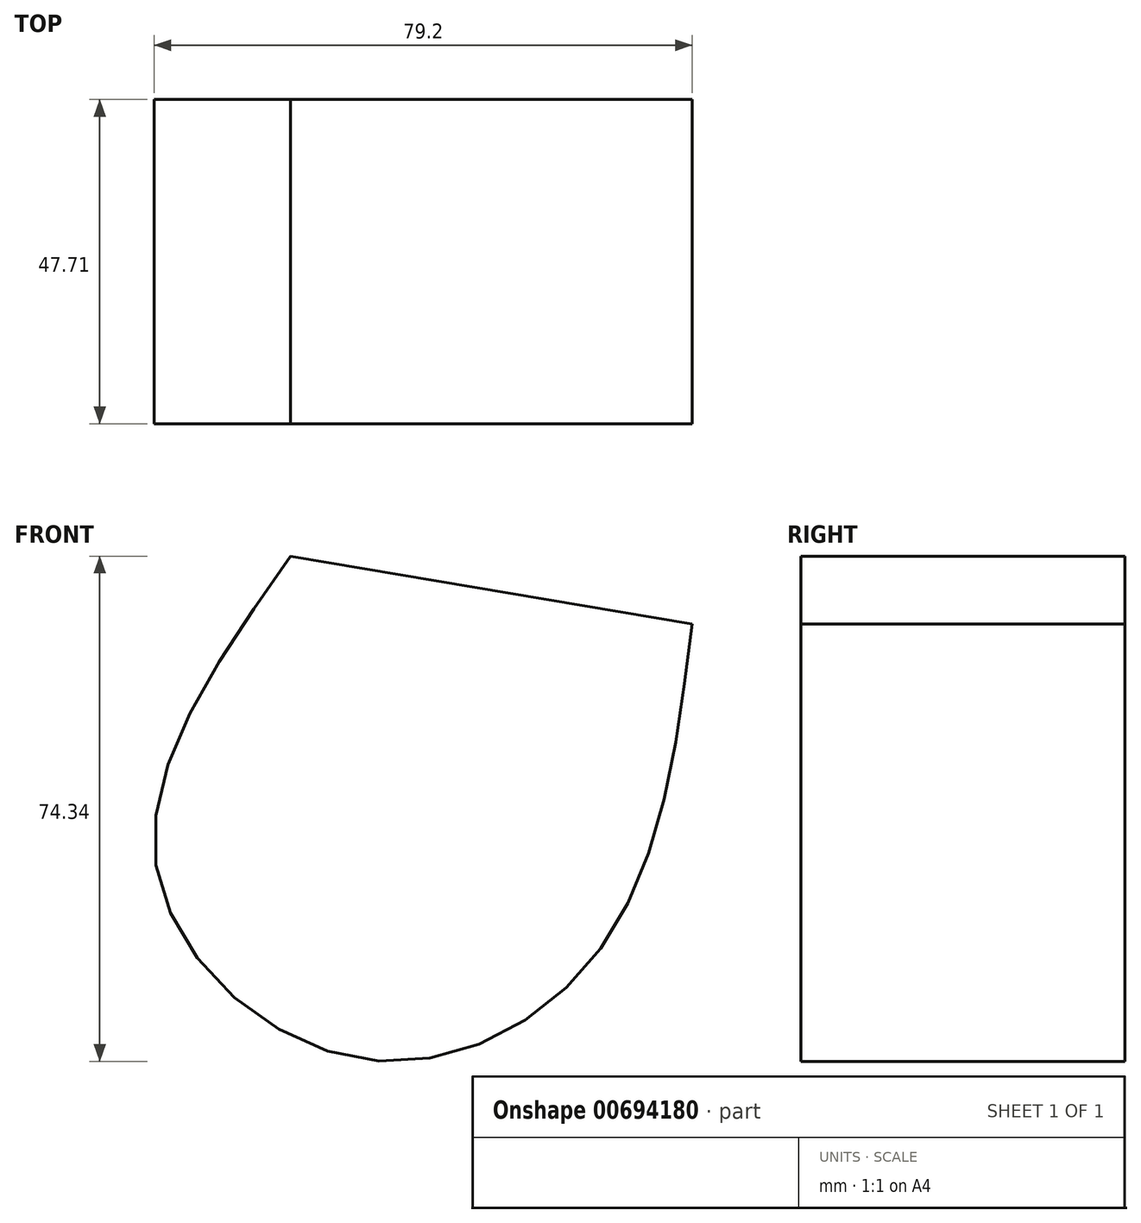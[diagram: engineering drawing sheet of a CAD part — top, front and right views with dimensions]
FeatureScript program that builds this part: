
annotation { "Feature Type Name" : "Feature", "Feature Type Description" : "" }
export const myFeature = defineFeature(function(context is Context, id is Id, definition is map)
    precondition{}
    {
        {
            var Q0;
            Q0=qCreatedBy(makeId("Front.planeOp"),FACE);
            var sketch = newSketch(context, id + "F0", { "sketchPlane" : qUnion([Q0])});
            skFitSpline(sketch, "E0", {"points": [v(-27.18, 23.86) * mm, v(-46.89, -22.2) * mm, v(-17.63, -50) * mm, v(18.05, -34.44) * mm, v(31.95, 13.9) * mm], "startDerivative": vector(-126.13, -178.37) * mm, "endDerivative": vector(25.2, 202.46) * mm});
            skLineSegment(sketch, "E1", {"start": v(31.95, 13.9) * mm, "end": v(-27.18, 23.86) * mm});
            skSolve(sketch);
        }
        {
            var Q0;
            Q0=makeQuery(id+"F0.imprint","IMPRINT",FACE,{"disambiguationData":[TD([[makeQuery(id+"F0.imprint","IMPRINT",EDGE,{"derivedFrom":sQuery(id+"F0.wireOp",EDGE,"E0")}),1.0]])]});
            extrude(context, id + "F1", {"entities" : qUnion([Q0]), "depth" : 47.7 * mm, "offsetDistance" : 25.4 * mm});
        }
    });
